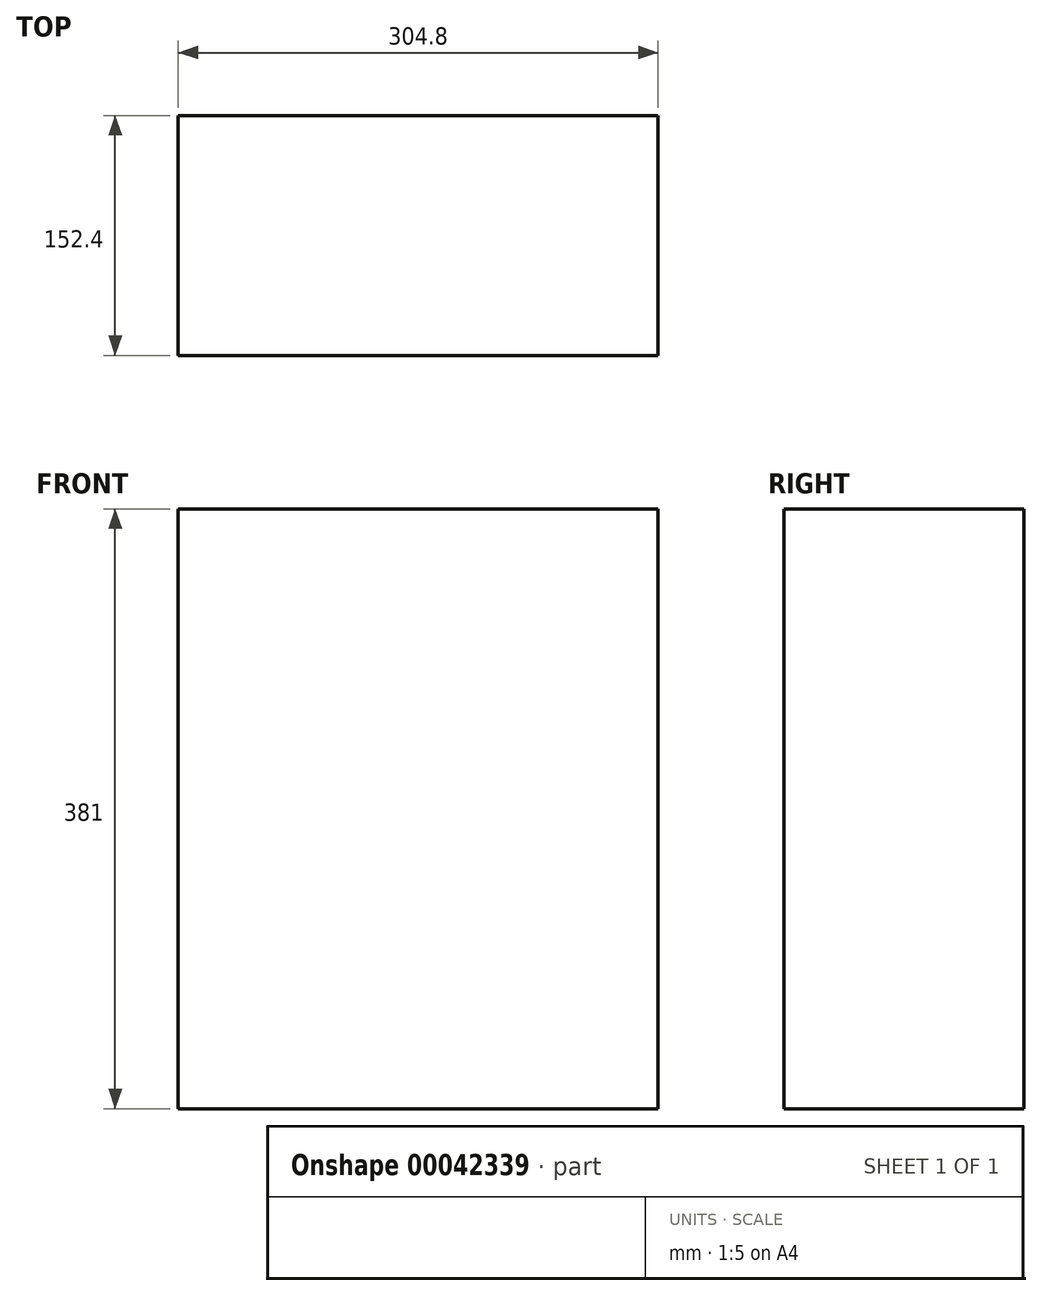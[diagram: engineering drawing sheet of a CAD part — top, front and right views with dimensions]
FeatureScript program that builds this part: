
annotation { "Feature Type Name" : "Feature", "Feature Type Description" : "" }
export const myFeature = defineFeature(function(context is Context, id is Id, definition is map)
    precondition{}
    {
        {
            var Q0;
            Q0=qCreatedBy(makeId("Front.planeOp"),FACE);
            var sketch = newSketch(context, id + "F0", { "sketchPlane" : qUnion([Q0])});
            skLineSegment(sketch, "E0.bottom", {"start": v(-143.36, 0) * mm, "end": v(161.44, 0) * mm});
            skLineSegment(sketch, "E0.top", {"start": v(-143.36, 381) * mm, "end": v(161.44, 381) * mm});
            skLineSegment(sketch, "E0.left", {"start": v(-143.36, 0) * mm, "end": v(-143.36, 381) * mm});
            skLineSegment(sketch, "E0.right", {"start": v(161.44, 0) * mm, "end": v(161.44, 381) * mm});
            skSolve(sketch);
        }
        {
            var Q0;
            Q0=makeQuery(id+"F0.imprint","IMPRINT",FACE,{"disambiguationData":[TD([[makeQuery(id+"F0.imprint","IMPRINT",EDGE,{"derivedFrom":sQuery(id+"F0.wireOp",EDGE,"E0.bottom")}),1.0]])]});
            extrude(context, id + "F1", {"entities" : qUnion([Q0]), "depth" : 152.4 * mm, "offsetDistance" : 25.4 * mm});
        }
    });
